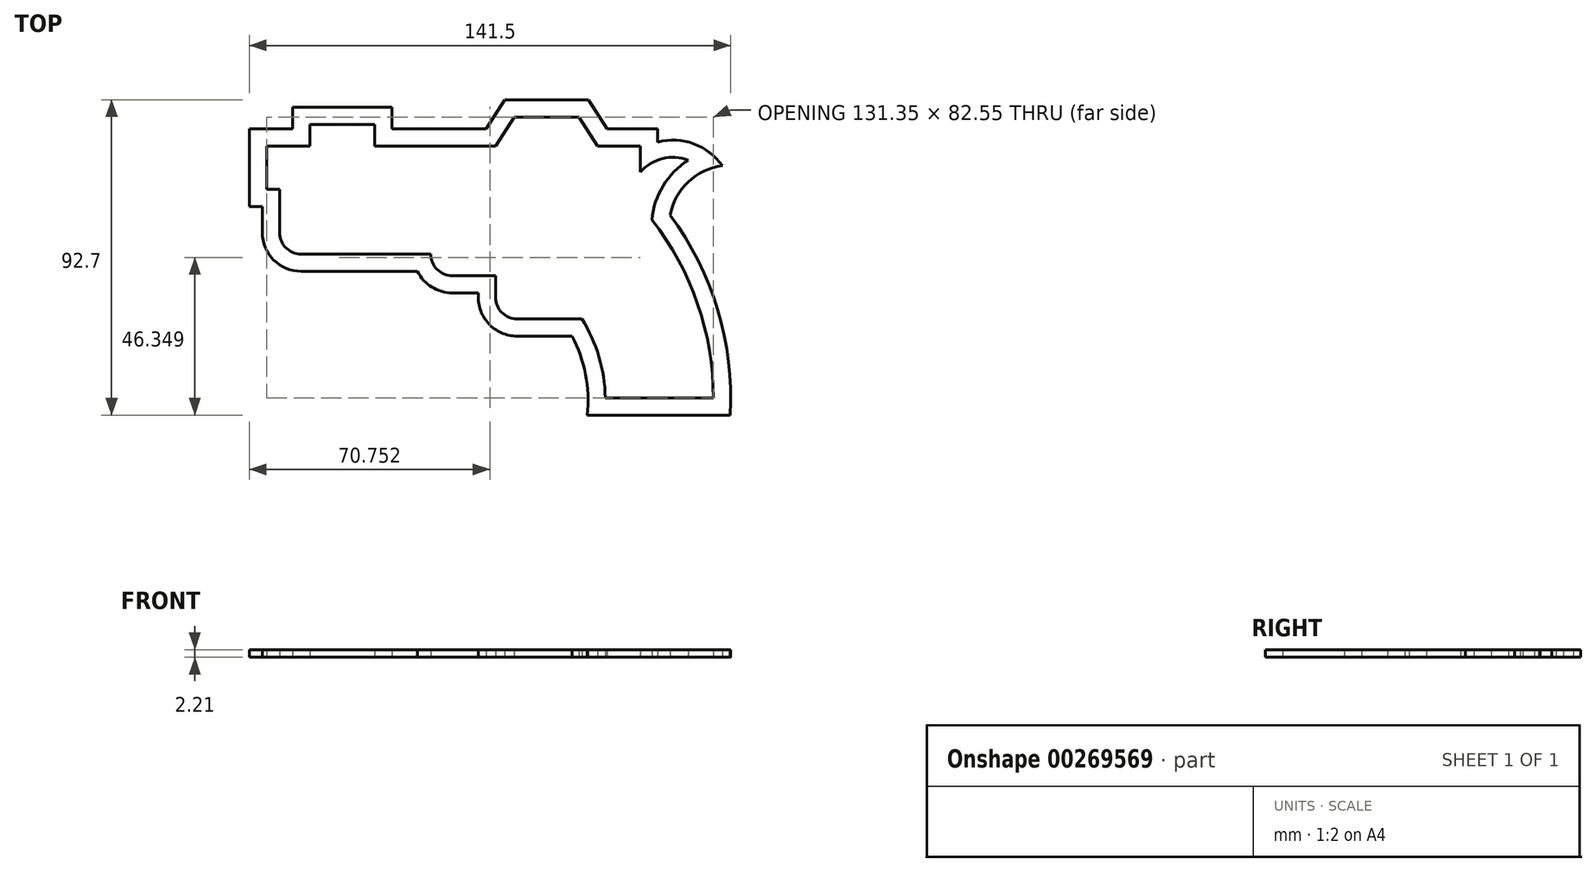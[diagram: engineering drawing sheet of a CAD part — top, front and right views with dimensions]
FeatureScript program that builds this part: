
annotation { "Feature Type Name" : "Feature", "Feature Type Description" : "" }
export const myFeature = defineFeature(function(context is Context, id is Id, definition is map)
    precondition{}
    {
        {
            var Q0;
            Q0=qCreatedBy(makeId("Top.planeOp"),FACE);
            var sketch = newSketch(context, id + "F0", { "sketchPlane" : qUnion([Q0])});
            skLineSegment(sketch, "E0", {"start": v(-14.2, -24.22) * mm, "end": v(17.54, -24.22) * mm});
            skArc(sketch, "E1", {"start": v(10.17, 45.63) * mm, "mid": v(2.6, 46.07) * mm, "end": v(-3.88, 42.15) * mm});
            skLineSegment(sketch, "E2", {"start": v(-3.88, 42.15) * mm, "end": v(-3.88, 49.77) * mm});
            skLineSegment(sketch, "E3", {"start": v(-3.88, 49.77) * mm, "end": v(-16.47, 49.77) * mm});
            skLineSegment(sketch, "E4", {"start": v(-16.47, 49.77) * mm, "end": v(-21.96, 58.32) * mm});
            skLineSegment(sketch, "E5", {"start": v(-21.96, 58.32) * mm, "end": v(-41, 58.32) * mm});
            skLineSegment(sketch, "E6", {"start": v(-41, 58.32) * mm, "end": v(-46.5, 49.77) * mm});
            skLineSegment(sketch, "E7", {"start": v(-46.5, 49.77) * mm, "end": v(-82.05, 49.77) * mm});
            skLineSegment(sketch, "E8", {"start": v(-82.05, 49.77) * mm, "end": v(-82.05, 56.12) * mm});
            skLineSegment(sketch, "E9", {"start": v(-82.05, 56.12) * mm, "end": v(-101.1, 56.12) * mm});
            skLineSegment(sketch, "E10", {"start": v(-101.1, 56.12) * mm, "end": v(-101.1, 49.77) * mm});
            skLineSegment(sketch, "E11", {"start": v(-101.1, 49.77) * mm, "end": v(-113.8, 49.77) * mm});
            skLineSegment(sketch, "E12", {"start": v(-113.8, 49.77) * mm, "end": v(-113.8, 37.07) * mm});
            skLineSegment(sketch, "E13", {"start": v(-113.8, 37.07) * mm, "end": v(-109.98, 37.07) * mm});
            skLineSegment(sketch, "E14", {"start": v(-109.98, 37.07) * mm, "end": v(-109.98, 24.37) * mm});
            skLineSegment(sketch, "E15", {"start": v(-103.63, 18.02) * mm, "end": v(-65.53, 18.02) * mm});
            skPoint(sketch, "E16.visualSharp", {"position": v(-109.98, 18.02) * mm});
            skArc(sketch, "E16.filletArc", {"start": v(-109.98, 24.37) * mm, "mid": v(-108.12, 19.88) * mm, "end": v(-103.63, 18.02) * mm});
            skLineSegment(sketch, "E17", {"start": v(-65.53, 18.02) * mm, "end": v(-65.53, 18.02) * mm});
            skLineSegment(sketch, "E18", {"start": v(-59.18, 11.67) * mm, "end": v(-46.48, 11.67) * mm});
            skPoint(sketch, "E19.visualSharp", {"position": v(-65.53, 11.67) * mm});
            skArc(sketch, "E19.filletArc", {"start": v(-65.53, 18.02) * mm, "mid": v(-63.67, 13.53) * mm, "end": v(-59.18, 11.67) * mm});
            skLineSegment(sketch, "E20", {"start": v(-46.48, 11.67) * mm, "end": v(-46.48, 5.32) * mm});
            skLineSegment(sketch, "E21", {"start": v(-40.13, -1.03) * mm, "end": v(-21.08, -1.03) * mm});
            skArc(sketch, "E22", {"start": v(-14.2, -24.22) * mm, "mid": v(-16.08, -12.16) * mm, "end": v(-21.08, -1.03) * mm});
            skPoint(sketch, "E23.visualSharp", {"position": v(-46.48, -1.03) * mm});
            skArc(sketch, "E23.filletArc", {"start": v(-46.48, 5.32) * mm, "mid": v(-44.62, 0.83) * mm, "end": v(-40.13, -1.03) * mm});
            skArc(sketch, "E24", {"start": v(17.54, -24.22) * mm, "mid": v(12.91, 3.45) * mm, "end": v(-0.48, 28.1) * mm});
            skArc(sketch, "E25", {"start": v(10.17, 45.63) * mm, "mid": v(2.8, 38.1) * mm, "end": v(-0.48, 28.1) * mm});
            skLineSegment(sketch, "E26.0", {"start": v(-76.97, 54.85) * mm, "end": v(-76.97, 61.2) * mm});
            skArc(sketch, "E26.1", {"start": v(-51.49, 6.6) * mm, "mid": v(-48.65, -2.3) * mm, "end": v(-40.13, -6.1) * mm});
            skLineSegment(sketch, "E26.2", {"start": v(-59.18, 6.6) * mm, "end": v(-51.49, 6.6) * mm});
            skArc(sketch, "E26.3", {"start": v(-69.42, 12.94) * mm, "mid": v(-65.2, 8.3) * mm, "end": v(-59.18, 6.6) * mm});
            skLineSegment(sketch, "E26.4", {"start": v(-103.63, 12.94) * mm, "end": v(-69.42, 12.94) * mm});
            skArc(sketch, "E26.5", {"start": v(-115.06, 24.37) * mm, "mid": v(-111.71, 16.29) * mm, "end": v(-103.63, 12.94) * mm});
            skLineSegment(sketch, "E26.6", {"start": v(-115.06, 32) * mm, "end": v(-115.06, 24.37) * mm});
            skLineSegment(sketch, "E26.7", {"start": v(-106.18, 61.2) * mm, "end": v(-106.18, 54.85) * mm});
            skLineSegment(sketch, "E26.8", {"start": v(-106.18, 54.85) * mm, "end": v(-118.88, 54.85) * mm});
            skLineSegment(sketch, "E26.9", {"start": v(-118.88, 54.85) * mm, "end": v(-118.88, 32) * mm});
            skLineSegment(sketch, "E26.10", {"start": v(-118.88, 32) * mm, "end": v(-115.06, 32) * mm});
            skLineSegment(sketch, "E26.11", {"start": v(-40.13, -6.1) * mm, "end": v(-24.01, -6.1) * mm});
            skLineSegment(sketch, "E26.12", {"start": v(-76.97, 61.2) * mm, "end": v(-106.18, 61.2) * mm});
            skArc(sketch, "E26.13", {"start": v(-19.49, -29.3) * mm, "mid": v(-20.03, -17.37) * mm, "end": v(-24.01, -6.1) * mm});
            skLineSegment(sketch, "E26.14", {"start": v(-19.49, -29.3) * mm, "end": v(22.48, -29.3) * mm});
            skArc(sketch, "E26.15", {"start": v(22.48, -29.3) * mm, "mid": v(18.83, 1.65) * mm, "end": v(4.84, 29.5) * mm});
            skArc(sketch, "E26.16", {"start": v(20.22, 44) * mm, "mid": v(10.2, 39.23) * mm, "end": v(4.84, 29.5) * mm});
            skArc(sketch, "E26.17", {"start": v(20.22, 44) * mm, "mid": v(11.8, 50.44) * mm, "end": v(1.2, 50.96) * mm});
            skLineSegment(sketch, "E26.18", {"start": v(1.2, 50.96) * mm, "end": v(1.2, 54.85) * mm});
            skLineSegment(sketch, "E26.19", {"start": v(1.2, 54.85) * mm, "end": v(-13.7, 54.85) * mm});
            skLineSegment(sketch, "E26.20", {"start": v(-13.7, 54.85) * mm, "end": v(-19.18, 63.4) * mm});
            skLineSegment(sketch, "E26.21", {"start": v(-19.18, 63.4) * mm, "end": v(-43.78, 63.4) * mm});
            skLineSegment(sketch, "E26.22", {"start": v(-43.78, 63.4) * mm, "end": v(-49.27, 54.85) * mm});
            skLineSegment(sketch, "E26.23", {"start": v(-49.27, 54.85) * mm, "end": v(-76.97, 54.85) * mm});
            skSolve(sketch);
        }
        {
            var Q0;
            Q0=makeQuery(id+"F0.imprint","IMPRINT",FACE,{"disambiguationData":[TD([[makeQuery(id+"F0.imprint","IMPRINT",EDGE,{"derivedFrom":sQuery(id+"F0.wireOp",EDGE,"E0")}),-1.0]])]});
            extrude(context, id + "F1", {"entities" : qUnion([Q0]), "depth" : 2.2 * mm});
        }
    });
